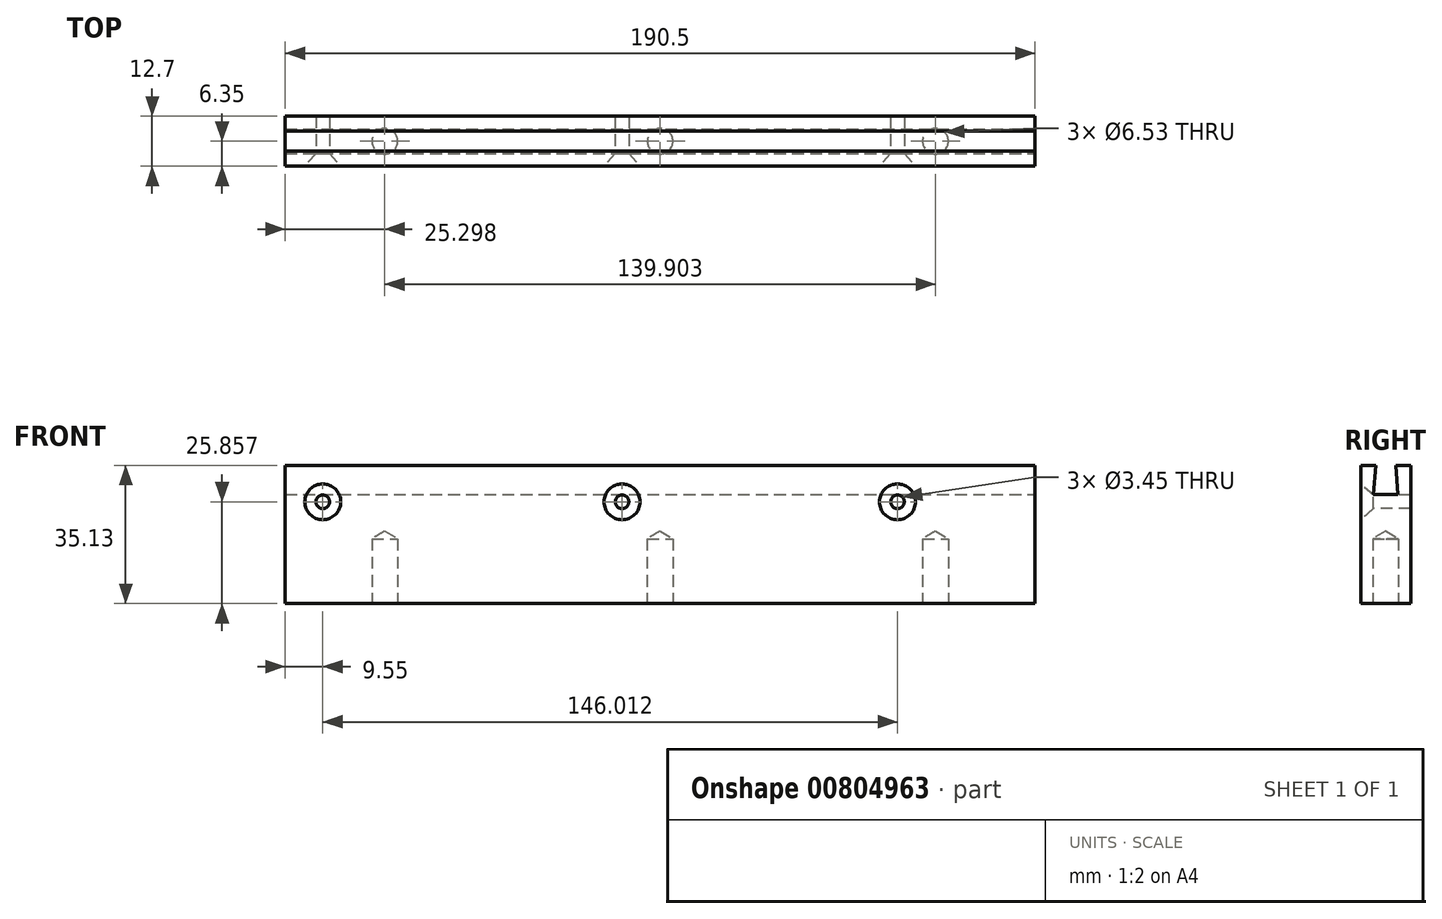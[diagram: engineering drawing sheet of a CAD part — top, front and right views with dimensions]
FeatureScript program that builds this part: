
annotation { "Feature Type Name" : "Feature", "Feature Type Description" : "" }
export const myFeature = defineFeature(function(context is Context, id is Id, definition is map)
    precondition{}
    {
        {
            var Q0;
            Q0=qCreatedBy(makeId("Front.planeOp"),FACE);
            var sketch = newSketch(context, id + "F0", { "sketchPlane" : qUnion([Q0])});
            skLineSegment(sketch, "E0.bottom", {"start": v(0, 0) * mm, "end": v(190.5, 0) * mm});
            skLineSegment(sketch, "E0.top", {"start": v(0, 35.13) * mm, "end": v(190.5, 35.13) * mm});
            skLineSegment(sketch, "E0.left", {"start": v(0, 0) * mm, "end": v(0, 35.13) * mm});
            skLineSegment(sketch, "E0.right", {"start": v(190.5, 0) * mm, "end": v(190.5, 35.13) * mm});
            skSolve(sketch);
        }
        {
            var Q0;
            Q0 = qSketchRegion(id + "F0", true);
            extrude(context, id + "F1", {"entities" : qUnion([Q0]), "depth" : 12.7 * mm, "offsetDistance" : 25.4 * mm});
        }
        {
            var Q0;
            Q0=makeQuery(id+"F1.opExtrude","SWEPT_FACE",FACE,{"disambiguationData":[OSD([sQuery(id+"F0.wireOp",EDGE,"E0.right")])]});
            var sketch = newSketch(context, id + "F2", { "sketchPlane" : qUnion([Q0])});
            skLineSegment(sketch, "E1", {"start": v(-8.9, 35.13) * mm, "end": v(-9.49, 27.76) * mm});
            skLineSegment(sketch, "E2", {"start": v(-9.49, 27.76) * mm, "end": v(-3.21, 27.76) * mm});
            skLineSegment(sketch, "E3", {"start": v(-3.21, 27.76) * mm, "end": v(-3.81, 35.13) * mm});
            skLineSegment(sketch, "E4", {"start": v(-3.81, 35.13) * mm, "end": v(-8.9, 35.13) * mm});
            skSolve(sketch);
        }
        {
            var Q0;
            Q0 = qSketchRegion(id + "F2", true);
            extrude(context, id + "F3", {"entities" : qUnion([Q0]), "operationType" : NewBodyOperationType.REMOVE, "endBound" : BoundingType.THROUGH_ALL, "oppositeDirection" : true, "depth" : 25.4 * mm, "offsetDistance" : 25.4 * mm});
        }
        {
            var Q0;
            Q0=makeQuery(id+"F1.opExtrude","CAP_FACE",FACE,{"disambiguationData":[OSD([sQuery(id+"F0.wireOp",EDGE,"E0.bottom"),sQuery(id+"F0.wireOp",EDGE,"E0.top"),sQuery(id+"F0.wireOp",EDGE,"E0.left"),sQuery(id+"F0.wireOp",EDGE,"E0.right")])],"isStart":false});
            var sketch = newSketch(context, id + "F4", { "sketchPlane" : qUnion([Q0])});
            skPoint(sketch, "E5", {"position": v(9.55, 25.86) * mm});
            skPoint(sketch, "E6", {"position": v(85.59, 25.86) * mm});
            skPoint(sketch, "E7", {"position": v(155.56, 25.86) * mm});
            skSolve(sketch);
        }
        {
            var Q0;
            Q0=sQuery(id+"F4.wireOp",VERTEX,"E5");
            var Q1;
            Q1=sQuery(id+"F4.wireOp",VERTEX,"E6");
            var Q2;
            Q2=sQuery(id+"F4.wireOp",VERTEX,"E7");
            var Q3;
            Q3=makeQuery(id+"F1.opExtrude","SWEPT_BODY",BODY,{"disambiguationData":[OSD([sQuery(id+"F0.wireOp",EDGE,"E0.bottom"),sQuery(id+"F0.wireOp",EDGE,"E0.top"),sQuery(id+"F0.wireOp",EDGE,"E0.left"),sQuery(id+"F0.wireOp",EDGE,"E0.right")])]});
            hole(context, id + "F5", {"style" : HoleStyle.C_SINK, "endStyle" : HoleEndStyle.THROUGH, "standardTappedOrClearance" : lookupTablePath({ "standard" : "ANSI", "engagement" : "75%", "pitch" : "32 tpi", "size" : "#8", "type" : "Tapped" }), "standardBlindInLast" : lookupTablePath({ "standard" : "ANSI", "engagement" : "75%", "pitch" : "32 tpi", "size" : "#8", "type" : "Tapped" }), "holeDiameter" : 3.45 * mm, "cSinkDiameter" : 9.12 * mm, "cSinkAngle" : 82 * degree, "majorDiameter" : 4.17 * mm, "showTappedDepth" : true, "isTappedThrough" : true, "tappedDepth" : 20.64 * mm, "tapClearance" : 3, "startFromSketch" : true, "locations" : qUnion([Q0, Q1, Q2]), "scope" : qUnion([Q3])});
        }
        {
            var Q0;
            Q0=makeQuery(id+"F1.opExtrude","SWEPT_FACE",FACE,{"disambiguationData":[OSD([sQuery(id+"F0.wireOp",EDGE,"E0.bottom")])]});
            var sketch = newSketch(context, id + "F6", { "sketchPlane" : qUnion([Q0])});
            skPoint(sketch, "E8", {"position": v(0, 6.35) * mm});
            skPoint(sketch, "E9", {"position": v(95.25, 12.7) * mm});
            skPoint(sketch, "E10", {"position": v(25.3, 6.35) * mm});
            skPoint(sketch, "E11", {"position": v(95.25, 6.35) * mm});
            skPoint(sketch, "E12", {"position": v(165.2, 6.35) * mm});
            skSolve(sketch);
        }
        {
            var Q0;
            Q0=sQuery(id+"F6.wireOp",VERTEX,"E10");
            var Q1;
            Q1=sQuery(id+"F6.wireOp",VERTEX,"E11");
            var Q2;
            Q2=sQuery(id+"F6.wireOp",VERTEX,"E12");
            var Q3;
            Q3=makeQuery(id+"F1.opExtrude","SWEPT_BODY",BODY,{"disambiguationData":[OSD([sQuery(id+"F0.wireOp",EDGE,"E0.bottom"),sQuery(id+"F0.wireOp",EDGE,"E0.top"),sQuery(id+"F0.wireOp",EDGE,"E0.left"),sQuery(id+"F0.wireOp",EDGE,"E0.right")])]});
            hole(context, id + "F7", {"style" : HoleStyle.SIMPLE, "endStyle" : HoleEndStyle.BLIND, "standardTappedOrClearance" : lookupTablePath({ "standard" : "ANSI", "engagement" : "75%", "pitch" : "18 tpi", "size" : "5/16", "type" : "Tapped" }), "standardBlindInLast" : lookupTablePath({ "standard" : "ANSI", "engagement" : "75%", "pitch" : "18 tpi", "size" : "5/16", "type" : "Tapped" }), "holeDiameter" : 6.53 * mm, "majorDiameter" : 7.94 * mm, "showTappedDepth" : true, "holeDepth" : 16.48 * mm, "isTappedThrough" : true, "tappedDepth" : 12.25 * mm, "tapClearance" : 3, "startFromSketch" : true, "locations" : qUnion([Q0, Q1, Q2]), "scope" : qUnion([Q3])});
        }
    });
